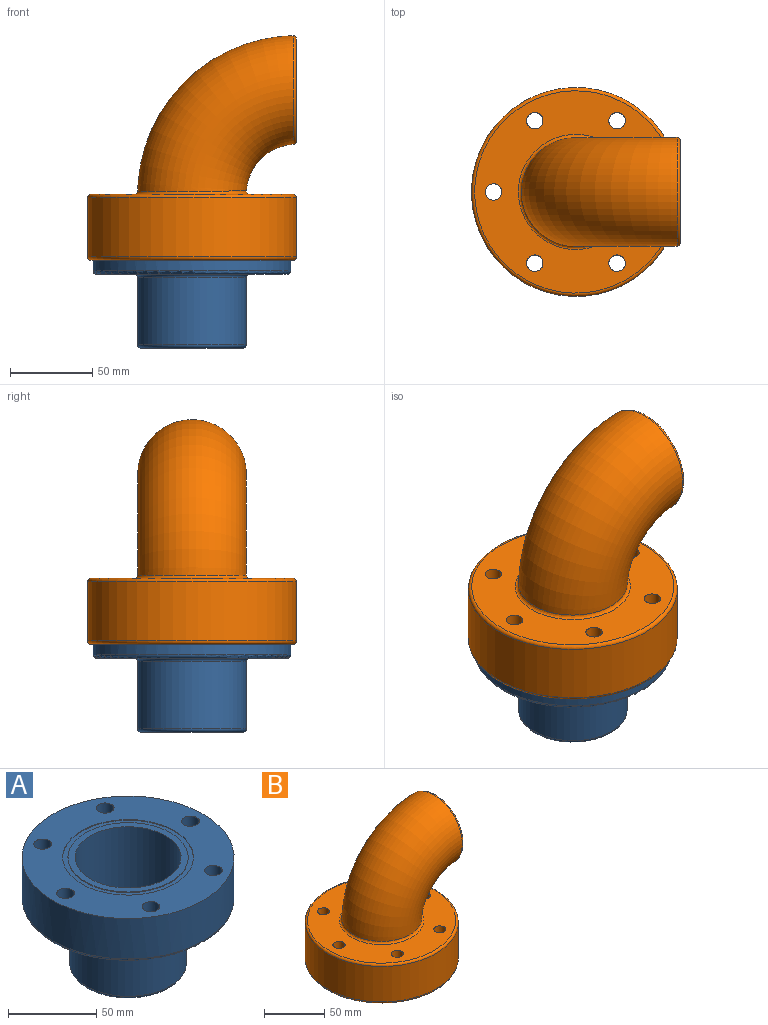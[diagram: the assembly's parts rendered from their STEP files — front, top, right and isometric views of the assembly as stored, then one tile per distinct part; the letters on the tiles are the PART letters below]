
ASSEMBLY  parts=2 mates=1
PART A: 19 faces, bbox 129.9x129.9x75 mm
  f0: plane 68x68mm, normal (0,0,1), area 804.2mm2, adj f1,f13
  f1: cylinder r=30mm len=75mm, axis (0,0,1), area 14137.2mm2, adj f0,f6
  f2: plane 120x120mm, normal (0,0,1), area 6537.7mm2, adj f3,f7,f8,f9,f10,f11,f12,f14
  f3: cylinder r=60mm len=120mm, axis (0,0,1), area 10555.8mm2, adj f2,f16
  f4: plane 116x116mm, normal (0,0,-1), area 6248.6mm2, adj f7,f8,f9,f10,f11,f12,f16,f17
  f5: cylinder r=33mm len=66mm, axis (0,0,1), area 8501.1mm2, adj f17,f18
  f6: plane 62x62mm, normal (0,0,-1), area 191.6mm2, adj f1,f18
  f7: cylinder r=5mm len=30mm, axis (0,0,1), area 942.5mm2, adj f2,f4
  f8: cylinder r=5mm len=30mm, axis (0,0,1), area 942.5mm2, adj f2,f4
  f9: cylinder r=5mm len=30mm, axis (0,0,1), area 942.5mm2, adj f2,f4
  f10: cylinder r=5mm len=30mm, axis (0,0,1), area 942.5mm2, adj f2,f4
  f11: cylinder r=5mm len=30mm, axis (0,0,1), area 942.5mm2, adj f2,f4
  f12: cylinder r=5mm len=30mm, axis (0,0,1), area 942.5mm2, adj f2,f4
  f13: cylinder r=34mm len=68mm, axis (0,0,1), area 106.8mm2, adj f0,f15
  f14: cylinder r=37mm len=74mm, axis (0,0,1), area 116.2mm2, adj f2,f15
  f15: plane 74x74mm, normal (0,0,1), area 669.2mm2, adj f13,f14
  f16: torus R=58mm, axis (0,0,-1), area 1170mm2, adj f3,f4
  f17: torus R=35mm, axis (0,0,-1), area 665.7mm2, adj f4,f5
  f18: torus R=31mm, axis (0,0,-1), area 637mm2, adj f5,f6
PART B: 23 faces, bbox 137.5x137.5x144.4 mm
  f0: plane 68x68mm, normal (0,0,-1), area 804.2mm2, adj f11,f13
  f1: cylinder r=60.5mm len=121mm, axis (0,0,1), area 5702mm2, adj f3,f4
  f2: cylinder r=63.5mm len=127mm, axis (0,0,1), area 14363.4mm2, adj f21,f22
  f3: plane 123x123mm, normal (0,0,-1), area 383.3mm2, adj f1,f22
  f4: plane 121x121mm, normal (0,0,-1), area 6726.9mm2, adj f1,f5,f6,f7,f8,f9,f10,f14
  f5: cylinder r=5mm len=25mm, axis (0,0,-1), area 785.4mm2, adj f4,f12
  f6: cylinder r=5mm len=25mm, axis (0,0,-1), area 785.4mm2, adj f4,f12
  f7: cylinder r=5mm len=25mm, axis (0,0,-1), area 785.4mm2, adj f4,f12
  f8: cylinder r=5mm len=25mm, axis (0,0,-1), area 785.4mm2, adj f4,f12
  f9: cylinder r=5mm len=25mm, axis (0,0,-1), area 785.4mm2, adj f4,f12
  f10: cylinder r=5mm len=25mm, axis (0,0,-1), area 785.4mm2, adj f4,f12
  f11: cylinder r=30mm len=60mm, axis (0,0,-1), area 4712.4mm2, adj f0,f16
  f12: plane 123x123mm, normal (0,0,1), area 7561.6mm2, adj f5,f6,f7,f8,f9,f10,f20,f21
  f13: cylinder r=34mm len=68mm, axis (0,0,1), area 106.8mm2, adj f0,f15
  f14: cylinder r=37mm len=74mm, axis (0,0,1), area 116.2mm2, adj f4,f15
  f15: plane 74x74mm, normal (0,0,-1), area 669.2mm2, adj f13,f14
  f16: torus R=63.5mm, axis (0,1,0), area 18801.6mm2, adj f11,f17
  f17: plane 62.05x62.01mm, normal (1,0,0), area 192.6mm2, adj f16,f19
  f18: torus R=63.5mm, axis (0,1,0), area 19852.4mm2, adj f19,f20
  f19: bspline ~66.09x66.02mm, area 633.3mm2, adj f17,f18
  f20: bspline ~70.06x70.02mm, area 670.6mm2, adj f12,f18
  f21: torus R=61.5mm, axis (0,0,1), area 1239.1mm2, adj f2,f12
  f22: torus R=61.5mm, axis (0,0,1), area 1239.1mm2, adj f2,f3
PLACE A t=(3.42,27.19,41.9)mm fixed
PLACE B t=(3.42,27.19,35.4)mm
MATE slider B.f1 <-> A.f1  axis (0,0,1) through (3.42,27.19,61.32)mm
